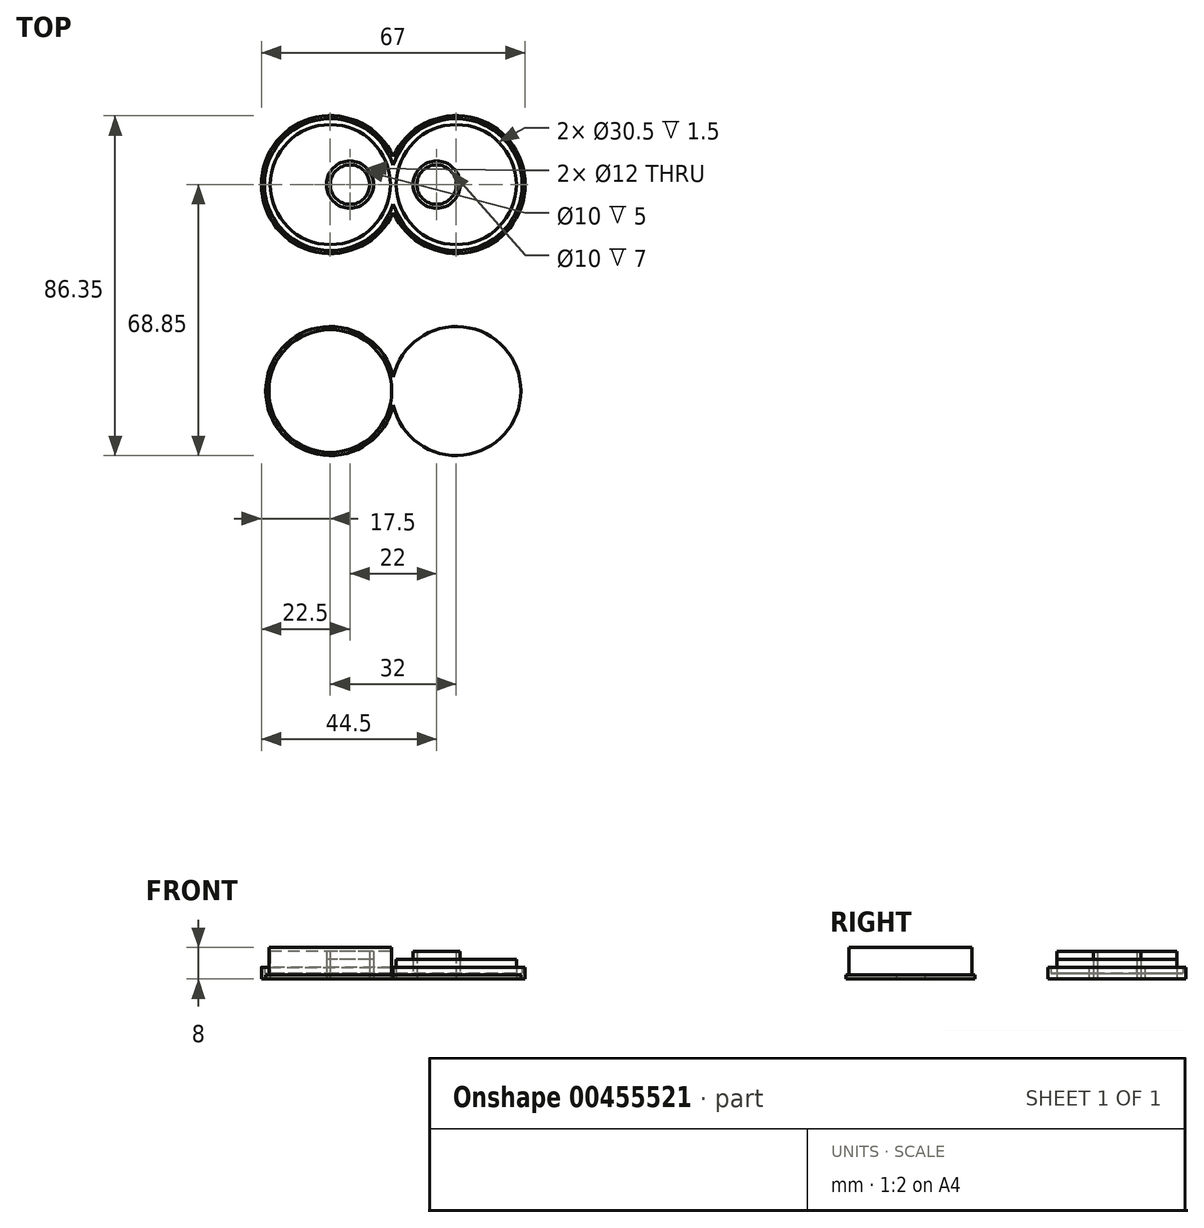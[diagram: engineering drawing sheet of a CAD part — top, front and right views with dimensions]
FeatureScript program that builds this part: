
annotation { "Feature Type Name" : "Feature", "Feature Type Description" : "" }
export const myFeature = defineFeature(function(context is Context, id is Id, definition is map)
    precondition{}
    {
        {
            var Q0;
            Q0=qCreatedBy(makeId("Top.planeOp"),FACE);
            var sketch = newSketch(context, id + "F0", { "sketchPlane" : qUnion([Q0])});
            skCircle(sketch, "E0", {"center": v(-11, 0) * mm, "radius": 5 * mm});
            skCircle(sketch, "E1", {"center": v(-11, 0) * mm, "radius": 6 * mm});
            skCircle(sketch, "E2", {"center": v(-16, 0) * mm, "radius": 16 * mm, "construction": true});
            skCircle(sketch, "E3", {"center": v(-16, 0) * mm, "radius": 15.25 * mm});
            skArc(sketch, "E4", {"start": v(0, 4.96) * mm, "mid": v(-32.75, 0) * mm, "end": v(0, -4.96) * mm});
            skLineSegment(sketch, "E5", {"start": v(0, 41.7) * mm, "end": v(0, 7.09) * mm});
            skCircle(sketch, "E6.MirrorC", {"center": v(11, 0) * mm, "radius": 5 * mm});
            skCircle(sketch, "E7.MirrorC", {"center": v(11, 0) * mm, "radius": 6 * mm});
            skCircle(sketch, "E8.MirrorC", {"center": v(16, 0) * mm, "radius": 15.25 * mm});
            skArc(sketch, "E9.MirrorC", {"start": v(0, 4.96) * mm, "mid": v(32.75, 0) * mm, "end": v(0, -4.96) * mm});
            skCircle(sketch, "E10.MirrorC", {"center": v(16, 0) * mm, "radius": 16 * mm, "construction": true});
            skArc(sketch, "E11.trimOffspring", {"start": v(0, 7.09) * mm, "mid": v(-33.5, 0) * mm, "end": v(0, -7.09) * mm});
            skArc(sketch, "E12.trimOffspring", {"start": v(0, 7.09) * mm, "mid": v(33.5, 0) * mm, "end": v(0, -7.09) * mm});
            skLineSegment(sketch, "E13.trimOffspring", {"start": v(0, -7.09) * mm, "end": v(0, -26.69) * mm});
            skLineSegment(sketch, "E14", {"start": v(-34.36, -26.22) * mm, "end": v(49.33, -26.22) * mm});
            skCircle(sketch, "E15.MirrorC", {"center": v(16, -52.45) * mm, "radius": 16 * mm, "construction": true});
            skArc(sketch, "E16.MirrorCS", {"start": v(0, -59.53) * mm, "mid": v(-33.5, -52.45) * mm, "end": v(0, -45.36) * mm});
            skArc(sketch, "E17.MirrorCS", {"start": v(0, -59.53) * mm, "mid": v(33.5, -52.45) * mm, "end": v(0, -45.36) * mm});
            skCircle(sketch, "E18.MirrorC", {"center": v(-16, -52.45) * mm, "radius": 16 * mm, "construction": true});
            skCircle(sketch, "E19.MirrorC", {"center": v(-16, -52.45) * mm, "radius": 15.6 * mm});
            skCircle(sketch, "E20", {"center": v(16, -52.45) * mm, "radius": 15.6 * mm});
            skArc(sketch, "E21", {"start": v(0, -48.85) * mm, "mid": v(-32.4, -52.45) * mm, "end": v(0, -56.05) * mm});
            skArc(sketch, "E22", {"start": v(0, -56.05) * mm, "mid": v(32.4, -52.45) * mm, "end": v(0, -48.85) * mm});
            skSolve(sketch);
        }
        {
            var Q0;
            Q0=makeQuery(id+"F0.imprint","IMPRINT",FACE,{"disambiguationData":[TD([[makeQuery(id+"F0.imprint","IMPRINT",EDGE,{"derivedFrom":sQuery(id+"F0.wireOp",EDGE,"E0")}),1.0]])]});
            var Q1;
            Q1=makeQuery(id+"F0.imprint","IMPRINT",FACE,{"disambiguationData":[TD([[makeQuery(id+"F0.imprint","IMPRINT",EDGE,{"derivedFrom":sQuery(id+"F0.wireOp",EDGE,"E6.MirrorC")}),-1.0]])]});
            var Q2;
            Q2=makeQuery(id+"F0.imprint","IMPRINT",FACE,{"disambiguationData":[TD([[makeQuery(id+"F0.imprint","IMPRINT",EDGE,{"derivedFrom":sQuery(id+"F0.wireOp",EDGE,"E1")}),-1.0]])]});
            var Q3;
            Q3=makeQuery(id+"F0.imprint","IMPRINT",FACE,{"disambiguationData":[TD([[makeQuery(id+"F0.imprint","IMPRINT",EDGE,{"derivedFrom":sQuery(id+"F0.wireOp",EDGE,"E7.MirrorC")}),1.0]])]});
            var Q4;
            Q4=makeQuery(id+"F0.imprint","IMPRINT",FACE,{"disambiguationData":[TD([[makeQuery(id+"F0.imprint","IMPRINT",EDGE,{"derivedFrom":sQuery(id+"F0.wireOp",EDGE,"E3")}),1.0]])]});
            var Q5;
            Q5=makeQuery(id+"F0.imprint","IMPRINT",FACE,{"disambiguationData":[TD([[makeQuery(id+"F0.imprint","IMPRINT",EDGE,{"derivedFrom":sQuery(id+"F0.wireOp",EDGE,"E0")}),1.0]])]});
            var Q6;
            Q6=makeQuery(id+"F0.imprint","IMPRINT",FACE,{"disambiguationData":[TD([[makeQuery(id+"F0.imprint","IMPRINT",EDGE,{"derivedFrom":sQuery(id+"F0.wireOp",EDGE,"E6.MirrorC")}),-1.0]])]});
            var Q7;
            Q7=sQuery(id+"F0.wireOp",EDGE,"E7.MirrorC");
            var Q8;
            Q8=sQuery(id+"F0.wireOp",EDGE,"E9.MirrorC");
            var Q9;
            Q9=sQuery(id+"F0.wireOp",EDGE,"E1");
            var Q10;
            Q10=sQuery(id+"F0.wireOp",EDGE,"E0");
            var Q11;
            Q11=sQuery(id+"F0.wireOp",EDGE,"E4");
            var Q12;
            Q12=sQuery(id+"F0.wireOp",EDGE,"E8.MirrorC");
            var Q13;
            Q13=sQuery(id+"F0.wireOp",EDGE,"E3");
            var Q14;
            Q14=sQuery(id+"F0.wireOp",EDGE,"E12.trimOffspring");
            var Q15;
            Q15=sQuery(id+"F0.wireOp",EDGE,"E11.trimOffspring");
            var Q16;
            Q16=sQuery(id+"F0.wireOp",EDGE,"E6.MirrorC");
            extrude(context, id + "F1", {"entities" : qUnion([Q0, Q1, Q2, Q3, Q4, Q5, Q6]), "surfaceEntities" : qUnion([Q7, Q8, Q9, Q10, Q11, Q12, Q13, Q14, Q15, Q16]), "depth" : 7 * mm});
        }
        {
            var Q0;
            Q0=makeQuery(id+"F0.imprint","IMPRINT",FACE,{"disambiguationData":[TD([[makeQuery(id+"F0.imprint","IMPRINT",EDGE,{"derivedFrom":sQuery(id+"F0.wireOp",EDGE,"E1")}),1.0]])]});
            var Q1;
            Q1=makeQuery(id+"F0.imprint","IMPRINT",FACE,{"disambiguationData":[TD([[makeQuery(id+"F0.imprint","IMPRINT",EDGE,{"derivedFrom":sQuery(id+"F0.wireOp",EDGE,"E7.MirrorC")}),-1.0]])]});
            extrude(context, id + "F2", {"entities" : qUnion([Q0, Q1]), "depth" : 5 * mm});
        }
        {
            var Q0;
            Q0=makeQuery(id+"F0.imprint","IMPRINT",FACE,{"disambiguationData":[TD([[makeQuery(id+"F0.imprint","IMPRINT",EDGE,{"derivedFrom":sQuery(id+"F0.wireOp",EDGE,"E3")}),-1.0]])]});
            extrude(context, id + "F3", {"entities" : qUnion([Q0]), "depth" : 1.5 * mm});
        }
        {
            var Q0;
            Q0=makeQuery(id+"F0.imprint","IMPRINT",FACE,{"disambiguationData":[TD([[makeQuery(id+"F0.imprint","IMPRINT",EDGE,{"derivedFrom":sQuery(id+"F0.wireOp",EDGE,"E4")}),-1.0]])]});
            extrude(context, id + "F4", {"entities" : qUnion([Q0]), "operationType" : NewBodyOperationType.ADD, "depth" : 3 * mm});
        }
        {
            var Q0;
            Q0=makeQuery(id+"F0.imprint","IMPRINT",FACE,{"disambiguationData":[TD([[makeQuery(id+"F0.imprint","IMPRINT",EDGE,{"derivedFrom":sQuery(id+"F0.wireOp",EDGE,"E19.MirrorC")}),1.0]])]});
            extrude(context, id + "F5", {"entities" : qUnion([Q0]), "depth" : 8 * mm});
        }
        {
            var Q0;
            Q0=makeQuery(id+"F0.imprint","IMPRINT",FACE,{"disambiguationData":[TD([[makeQuery(id+"F0.imprint","IMPRINT",EDGE,{"derivedFrom":sQuery(id+"F0.wireOp",EDGE,"E19.MirrorC")}),-1.0]])]});
            var Q1;
            Q1=makeQuery(id+"F0.imprint","IMPRINT",FACE,{"disambiguationData":[TD([[makeQuery(id+"F0.imprint","IMPRINT",EDGE,{"derivedFrom":sQuery(id+"F0.wireOp",EDGE,"E20")}),1.0]])]});
            var Q2;
            Q2=makeQuery(id+"F0.imprint","IMPRINT",FACE,{"disambiguationData":[TD([[makeQuery(id+"F0.imprint","IMPRINT",EDGE,{"derivedFrom":sQuery(id+"F0.wireOp",EDGE,"E16.MirrorCS")}),-1.0]])]});
            extrude(context, id + "F6", {"entities" : qUnion([Q0, Q1, Q2]), "operationType" : NewBodyOperationType.ADD, "depth" : 1 * mm});
        }
    });
